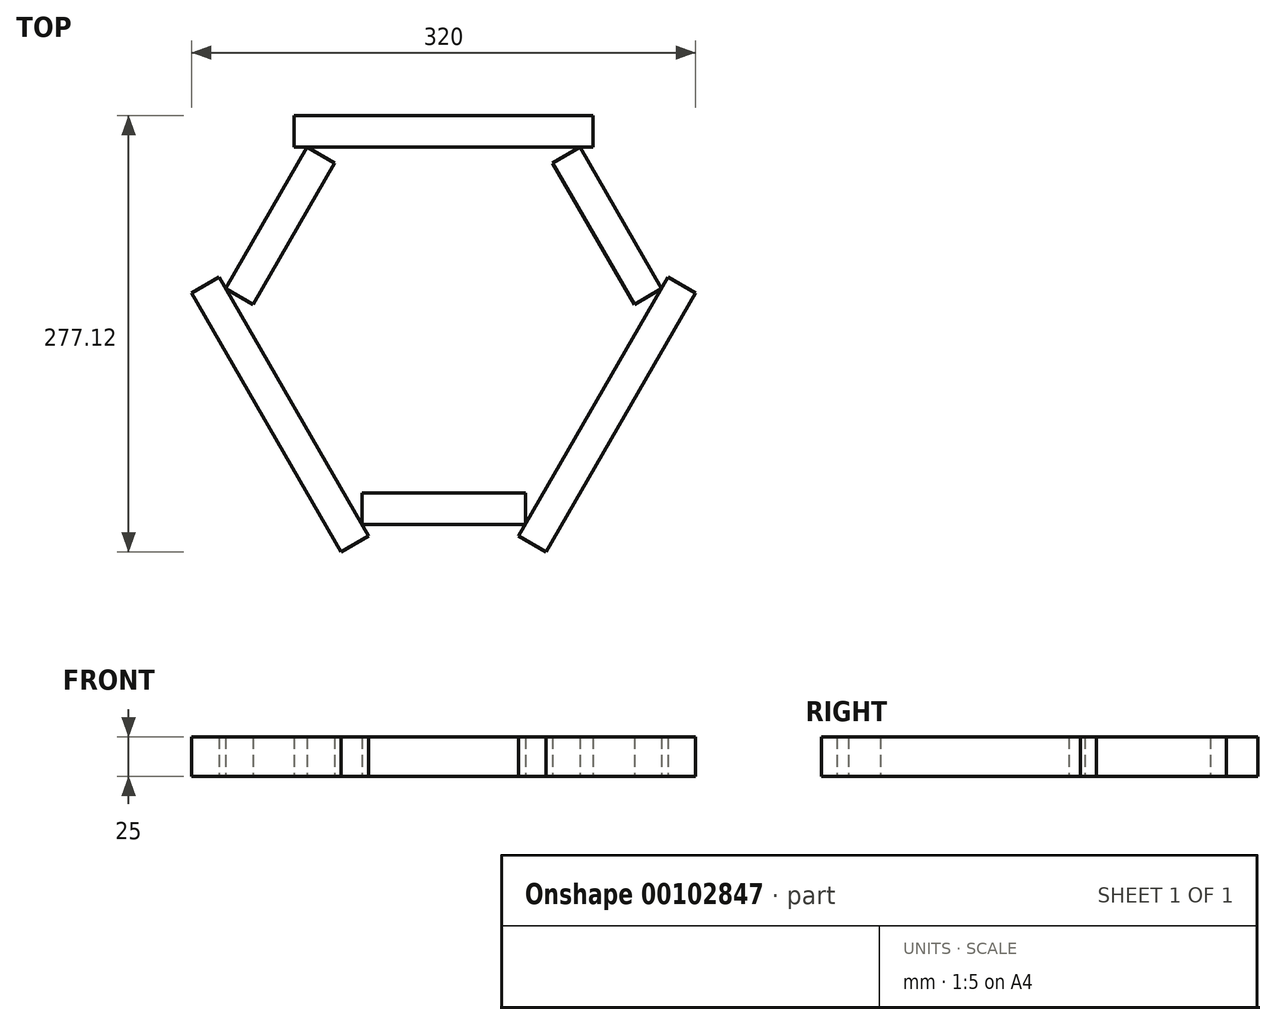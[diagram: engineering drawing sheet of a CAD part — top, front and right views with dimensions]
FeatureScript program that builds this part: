
annotation { "Feature Type Name" : "Feature", "Feature Type Description" : "" }
export const myFeature = defineFeature(function(context is Context, id is Id, definition is map)
    precondition{}
    {
        {
            var Q0;
            Q0=qCreatedBy(makeId("Top.planeOp"),FACE);
            var sketch = newSketch(context, id + "F0", { "sketchPlane" : qUnion([Q0])});
            skCircle(sketch, "E0.cCircle", {"center": v(0, 0) * mm, "radius": 150 * mm, "construction": true});
            skLineSegment(sketch, "E0.0", {"start": v(-150, 0) * mm, "end": v(-75, 129.9) * mm, "construction": true});
            skLineSegment(sketch, "E0.1", {"start": v(-75, 129.9) * mm, "end": v(75, 129.9) * mm, "construction": true});
            skLineSegment(sketch, "E0.2", {"start": v(75, 129.9) * mm, "end": v(150, 0) * mm, "construction": true});
            skLineSegment(sketch, "E0.3", {"start": v(150, 0) * mm, "end": v(75, -129.9) * mm, "construction": true});
            skLineSegment(sketch, "E0.4", {"start": v(75, -129.9) * mm, "end": v(-75, -129.9) * mm, "construction": true});
            skLineSegment(sketch, "E0.5", {"start": v(-75, -129.9) * mm, "end": v(-150, 0) * mm, "construction": true});
            skLineSegment(sketch, "E1", {"start": v(0, 129.9) * mm, "end": v(-95, 129.9) * mm});
            skLineSegment(sketch, "E2", {"start": v(-95, 129.9) * mm, "end": v(-95, 109.9) * mm});
            skLineSegment(sketch, "E3", {"start": v(-95, 109.9) * mm, "end": v(95, 109.9) * mm});
            skLineSegment(sketch, "E4", {"start": v(95, 109.9) * mm, "end": v(95, 129.9) * mm});
            skLineSegment(sketch, "E5", {"start": v(95, 129.9) * mm, "end": v(0, 129.9) * mm});
            skLineSegment(sketch, "E6", {"start": v(-112.5, -64.95) * mm, "end": v(-160, 17.32) * mm});
            skLineSegment(sketch, "E7", {"start": v(-160, 17.32) * mm, "end": v(-142.68, 27.32) * mm});
            skLineSegment(sketch, "E8", {"start": v(-142.68, 27.32) * mm, "end": v(-47.68, -137.22) * mm});
            skLineSegment(sketch, "E9", {"start": v(-47.68, -137.22) * mm, "end": v(-65, -147.22) * mm});
            skLineSegment(sketch, "E10", {"start": v(-65, -147.22) * mm, "end": v(-112.5, -64.95) * mm});
            skLineSegment(sketch, "E11", {"start": v(112.5, -64.95) * mm, "end": v(160, 17.32) * mm});
            skLineSegment(sketch, "E12", {"start": v(160, 17.32) * mm, "end": v(142.68, 27.32) * mm});
            skLineSegment(sketch, "E13", {"start": v(142.68, 27.32) * mm, "end": v(47.68, -137.22) * mm});
            skLineSegment(sketch, "E14", {"start": v(47.68, -137.22) * mm, "end": v(65, -147.22) * mm});
            skLineSegment(sketch, "E15", {"start": v(65, -147.22) * mm, "end": v(112.5, -64.95) * mm});
            skLineSegment(sketch, "E16", {"start": v(138.45, 20) * mm, "end": v(121.13, 10) * mm});
            skLineSegment(sketch, "E17", {"start": v(86.55, 109.9) * mm, "end": v(69.23, 99.9) * mm});
            skLineSegment(sketch, "E18", {"start": v(69.23, 99.9) * mm, "end": v(121.13, 10) * mm});
            skLineSegment(sketch, "E19", {"start": v(86.55, 109.9) * mm, "end": v(138.45, 20) * mm});
            skLineSegment(sketch, "E20", {"start": v(-86.55, 109.9) * mm, "end": v(-69.23, 99.9) * mm});
            skLineSegment(sketch, "E21", {"start": v(-138.45, 20) * mm, "end": v(-121.13, 10) * mm});
            skLineSegment(sketch, "E22", {"start": v(-121.13, 10) * mm, "end": v(-69.23, 99.9) * mm});
            skLineSegment(sketch, "E23", {"start": v(-86.55, 109.9) * mm, "end": v(-138.45, 20) * mm});
            skLineSegment(sketch, "E24", {"start": v(-51.9, -129.9) * mm, "end": v(-51.9, -109.9) * mm});
            skLineSegment(sketch, "E25", {"start": v(51.9, -129.9) * mm, "end": v(51.9, -109.9) * mm});
            skLineSegment(sketch, "E26", {"start": v(51.9, -109.9) * mm, "end": v(-51.9, -109.9) * mm});
            skLineSegment(sketch, "E27", {"start": v(51.9, -129.9) * mm, "end": v(-51.9, -129.9) * mm});
            skLineSegment(sketch, "E28", {"start": v(-112.5, 64.95) * mm, "end": v(-65, 147.22) * mm});
            skLineSegment(sketch, "E29", {"start": v(-65, 147.22) * mm, "end": v(-47.68, 137.22) * mm});
            skLineSegment(sketch, "E30", {"start": v(-47.68, 137.22) * mm, "end": v(-142.68, -27.32) * mm});
            skLineSegment(sketch, "E31", {"start": v(-142.68, -27.32) * mm, "end": v(-160, -17.32) * mm});
            skLineSegment(sketch, "E32", {"start": v(-160, -17.32) * mm, "end": v(-112.5, 64.95) * mm});
            skLineSegment(sketch, "E33", {"start": v(0, -129.9) * mm, "end": v(-95, -129.9) * mm});
            skLineSegment(sketch, "E34", {"start": v(-95, -129.9) * mm, "end": v(-95, -109.9) * mm});
            skLineSegment(sketch, "E35", {"start": v(-95, -109.9) * mm, "end": v(95, -109.9) * mm});
            skLineSegment(sketch, "E36", {"start": v(95, -109.9) * mm, "end": v(95, -129.9) * mm});
            skLineSegment(sketch, "E37", {"start": v(95, -129.9) * mm, "end": v(0, -129.9) * mm});
            skSolve(sketch);
        }
        {
            var Q0;
            Q0=makeQuery(id+"F0.imprint","IMPRINT",FACE,{"disambiguationData":[TD([[makeQuery(id+"F0.imprint","IMPRINT",EDGE,{"derivedFrom":sQuery(id+"F0.wireOp",EDGE,"E1")}),1.0]])]});
            var Q1;
            Q1=makeQuery(id+"F0.imprint","IMPRINT",FACE,{"disambiguationData":[TD([[makeQuery(id+"F0.imprint","IMPRINT",EDGE,{"derivedFrom":sQuery(id+"F0.wireOp",EDGE,"E20")}),-1.0]])]});
            var Q2;
            Q2=makeQuery(id+"F0.imprint","IMPRINT",FACE,{"disambiguationData":[TD([[makeQuery(id+"F0.imprint","IMPRINT",EDGE,{"derivedFrom":sQuery(id+"F0.wireOp",EDGE,"E6")}),-1.0]])]});
            var Q3;
            Q3=makeQuery(id+"F0.imprint","IMPRINT",FACE,{"disambiguationData":[TD([[makeQuery(id+"F0.imprint","IMPRINT",EDGE,{"derivedFrom":sQuery(id+"F0.wireOp",EDGE,"E24")}),-1.0]])]});
            var Q4;
            Q4=makeQuery(id+"F0.imprint","IMPRINT",FACE,{"disambiguationData":[TD([[makeQuery(id+"F0.imprint","IMPRINT",EDGE,{"derivedFrom":sQuery(id+"F0.wireOp",EDGE,"E11")}),1.0]])]});
            var Q5;
            Q5=makeQuery(id+"F0.imprint","IMPRINT",FACE,{"disambiguationData":[TD([[makeQuery(id+"F0.imprint","IMPRINT",EDGE,{"derivedFrom":sQuery(id+"F0.wireOp",EDGE,"E16")}),-1.0]])]});
            var Q6;
            {var subQ0=sQuery(id+"F0.wireOp",EDGE,"E4");Q6=makeQuery(id+"F0.imprint","IMPRINT",FACE,{"disambiguationData":[TD([[makeQuery(id+"F0.imprint","IMPRINT",EDGE,{"derivedFrom":subQ0}),1.0]])]});}
            var Q7;
            {var subQ0=sQuery(id+"F0.wireOp",EDGE,"E9");Q7=makeQuery(id+"F0.imprint","IMPRINT",FACE,{"disambiguationData":[TD([[makeQuery(id+"F0.imprint","IMPRINT",EDGE,{"derivedFrom":subQ0}),-1.0]])]});}
            var Q8;
            {var subQ1=sQuery(id+"F0.wireOp",EDGE,"E6");var subQ5=sQuery(id+"F0.wireOp",EDGE,"E10");var subQ6=makeQuery(id+"F0.imprint","INTERSECT",VERTEX,{"derivedFrom":[subQ1,subQ5]});Q8=makeQuery(id+"F0.imprint","IMPRINT",FACE,{"disambiguationData":[TD([[makeQuery(id+"F0.imprint","IMPRINT",EDGE,{"disambiguationData":[TD([[subQ6,-1.0]])],"derivedFrom":subQ1}),-1.0]])]});}
            var Q9;
            {var subQ0=sQuery(id+"F0.wireOp",EDGE,"E33");var subQ5=sQuery(id+"F0.wireOp",EDGE,"E10");var subQ6=makeQuery(id+"F0.imprint","INTERSECT",VERTEX,{"derivedFrom":[subQ5,subQ0]});Q9=makeQuery(id+"F0.imprint","IMPRINT",FACE,{"disambiguationData":[TD([[makeQuery(id+"F0.imprint","IMPRINT",EDGE,{"disambiguationData":[TD([[subQ6,-1.0]])],"derivedFrom":subQ5}),-1.0]])]});}
            var Q10;
            {var subQ0=sQuery(id+"F0.wireOp",EDGE,"E37");var subQ5=sQuery(id+"F0.wireOp",EDGE,"E15");var subQ6=makeQuery(id+"F0.imprint","INTERSECT",VERTEX,{"derivedFrom":[subQ5,subQ0]});Q10=makeQuery(id+"F0.imprint","IMPRINT",FACE,{"disambiguationData":[TD([[makeQuery(id+"F0.imprint","IMPRINT",EDGE,{"disambiguationData":[TD([[subQ6,-1.0]])],"derivedFrom":subQ5}),1.0]])]});}
            var Q11;
            {var subQ0=sQuery(id+"F0.wireOp",EDGE,"E14");Q11=makeQuery(id+"F0.imprint","IMPRINT",FACE,{"disambiguationData":[TD([[makeQuery(id+"F0.imprint","IMPRINT",EDGE,{"derivedFrom":subQ0}),1.0]])]});}
            extrude(context, id + "F1", {"entities" : qUnion([Q0, Q1, Q2, Q3, Q4, Q5, Q6, Q7, Q8, Q9, Q10, Q11]), "depth" : 25 * mm});
        }
    });
